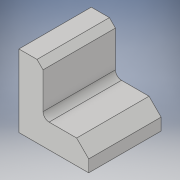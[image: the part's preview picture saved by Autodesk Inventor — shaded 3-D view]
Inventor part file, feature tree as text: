
AUTODESK INVENTOR PART (.ipt)
format: ipt  version: 2018 (Build 220112000, 112)  size: 109,056 bytes
history: native  units: in
note: dims shown in document units (in); Inventor stores cm internally (conversion verified against a paired STEP export)
features: chamfer x2, extrude x1, fillet x1, sketch x1
ambient origin geometry x8: Origin, YZ Plane, XZ Plane, XY Plane, X Axis, Y Axis, Z Axis, Center Point
bodies: Solid1 (feature_tree)
feature tree (5):
  extrude  "Extrusion1"  Depth=0.5in
  chamfer  "Chamfer1"  Distance=1.0in
  chamfer  "Chamfer2"  Distance=1.5in
  fillet  "Fillet2"  Radius=0.125in
  sketch  "Sketch1"  dims[d0=1.5in d1=0.5in d2=1.0in d3=1.5in d4=0.0in d6=0.125in d7=0.125in d8=45.0deg d9=0.25in d10=0.125in d11=45.0deg d12=0.125in]
